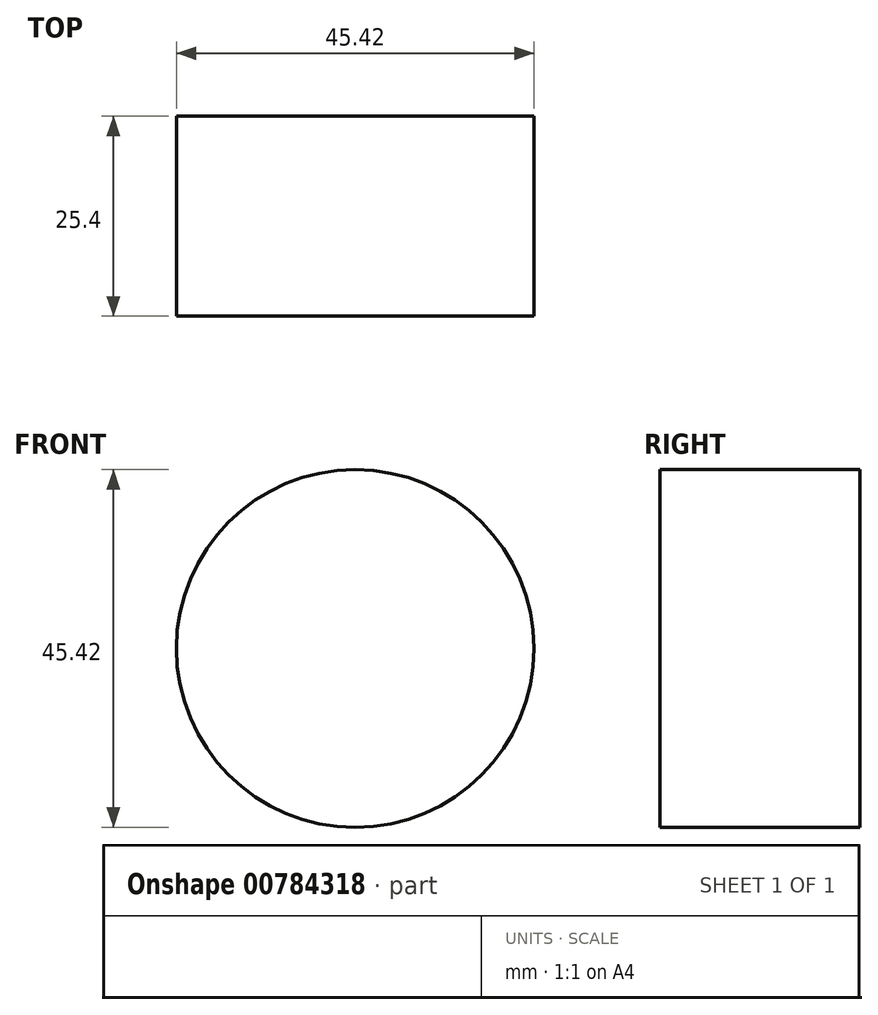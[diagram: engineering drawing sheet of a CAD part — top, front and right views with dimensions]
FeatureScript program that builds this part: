
annotation { "Feature Type Name" : "Feature", "Feature Type Description" : "" }
export const myFeature = defineFeature(function(context is Context, id is Id, definition is map)
    precondition{}
    {
        {
            var Q0;
            Q0=qCreatedBy(makeId("Front.planeOp"),FACE);
            var sketch = newSketch(context, id + "F0", { "sketchPlane" : qUnion([Q0])});
            skCircle(sketch, "E0", {"center": v(0, 0) * mm, "radius": 22.71 * mm});
            skSolve(sketch);
        }
        {
            var Q0;
            Q0=qCreatedBy(makeId("Top.planeOp"),FACE);
            var sketch = newSketch(context, id + "F1", { "sketchPlane" : qUnion([Q0])});
            skSolve(sketch);
        }
        {
            var Q0;
            Q0 = qSketchRegion(id + "F1", true);
            var Q1;
            Q1=makeQuery(id+"F0.imprint","IMPRINT",FACE,{"disambiguationData":[TD([[makeQuery(id+"F0.imprint","IMPRINT",EDGE,{"derivedFrom":sQuery(id+"F0.wireOp",EDGE,"E0")}),1.0]])]});
            extrude(context, id + "F2", {"entities" : qUnion([Q0, Q1]), "depth" : 25.4 * mm, "offsetDistance" : 25.4 * mm});
        }
    });
